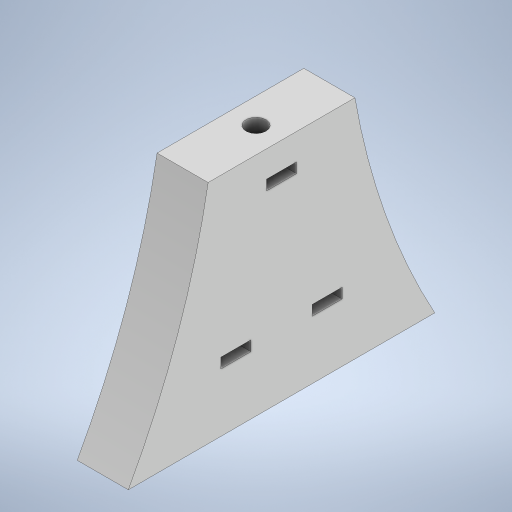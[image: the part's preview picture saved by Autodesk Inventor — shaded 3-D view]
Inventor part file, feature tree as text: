
AUTODESK INVENTOR PART (.ipt)
format: ipt  version: 2023.2 (Build 272271030, 271C)  size: 266,752 bytes
history: native  units: mm
features: extrude x4, sketch x4, projected_geometry x3
ambient origin geometry x8: Origin, YZ Plane, XZ Plane, XY Plane, X Axis, Y Axis, Z Axis, Center Point
bodies: Solid1 (feature_tree)
feature tree (11):
  extrude  "Extrusion1"  Depth=62.0mm
  extrude  "Extrusion2"  Depth=14.0mm TaperAngle=0.0deg
  extrude  "Extrusion3"  Depth=2.8mm
  extrude  "Extrusion4"  Depth=25.0mm
  sketch  "Sketch1"  dims[d0=400.0mm d1=62.0mm]
  sketch  "Sketch2"  dims[d2=84.0mm d4=14.0mm d5=0.0mm]
  projected_geometry  "Projected Loop1"
  sketch  "Sketch3"  dims[d6=8.2mm d7=2.8mm]
  projected_geometry  "Projected Loop2"
  sketch  "Sketch4"  dims[d8=16.0mm d9=25.0mm d10=14.0mm d11=0.0mm d12=5.5mm d13=25.0mm d14=25.0mm d15=0.0mm d16=8.2mm d17=2.8mm d19=10.0mm d20=5.5mm d21=15.0mm d22=0.0mm d23=40.228909mm]
  projected_geometry  "Projected Loop3"
